# Revit family: Triturador_XM-72_GENERADO
name_source: partatom
category: Equipos especializados
revit_build: Autodesk Revit 2016 (Build: 20151007_0715(x64)
units: mm (PartAtom-declared; Revit-internal decimal feet)

## family parameters
Compartido = No
Corte con vacíos al cargar = No
Cota de conector redondo = Diámetro de uso
Número OmniClass = 23.21.21.31.11
Punto de cálculo de habitación = No
Se basa en plano de trabajo = No
Siempre vertical = Sí
Tipo de pieza = Normal

## types (4) — shared parameters
Comentarios de tipo = Professional immersion blender. 750 W.
Cycle = 50 Hz
Fabricante = SAMMIC S.L.
Foodservice Equipment Identifier = Sí
Phase = 1
Revision Code = 1
Specification by Manufacturer = Fixed speed motor block.
630 mm detachable arm.
Designed for continuous use in recipients of up to 250 litres.
URL = https://www.sammic.com
URL Cutsheet = http://www.sammic.com
Weight in Pounds = 11.7

## per-type parameters (varying)
| type | FL Amps | Modelo | Volts |
| Immersion blender XM-72 230/50-60/1 | 5 A | 3030850 | 230 V |
| Immersion blender XM-72 120/50-60/1 MX | 5 A | 3030854 | 120 V |
| Immersion blender XM-72 230/50-60/1 AUS | 4 A | 3030852 | 230 V |
| Immersion blender XM-72 120/50-60/1 USA | 5 A | 3030858 | 120 V |

note: column(s) folded — value = type name in every type: Descripción
